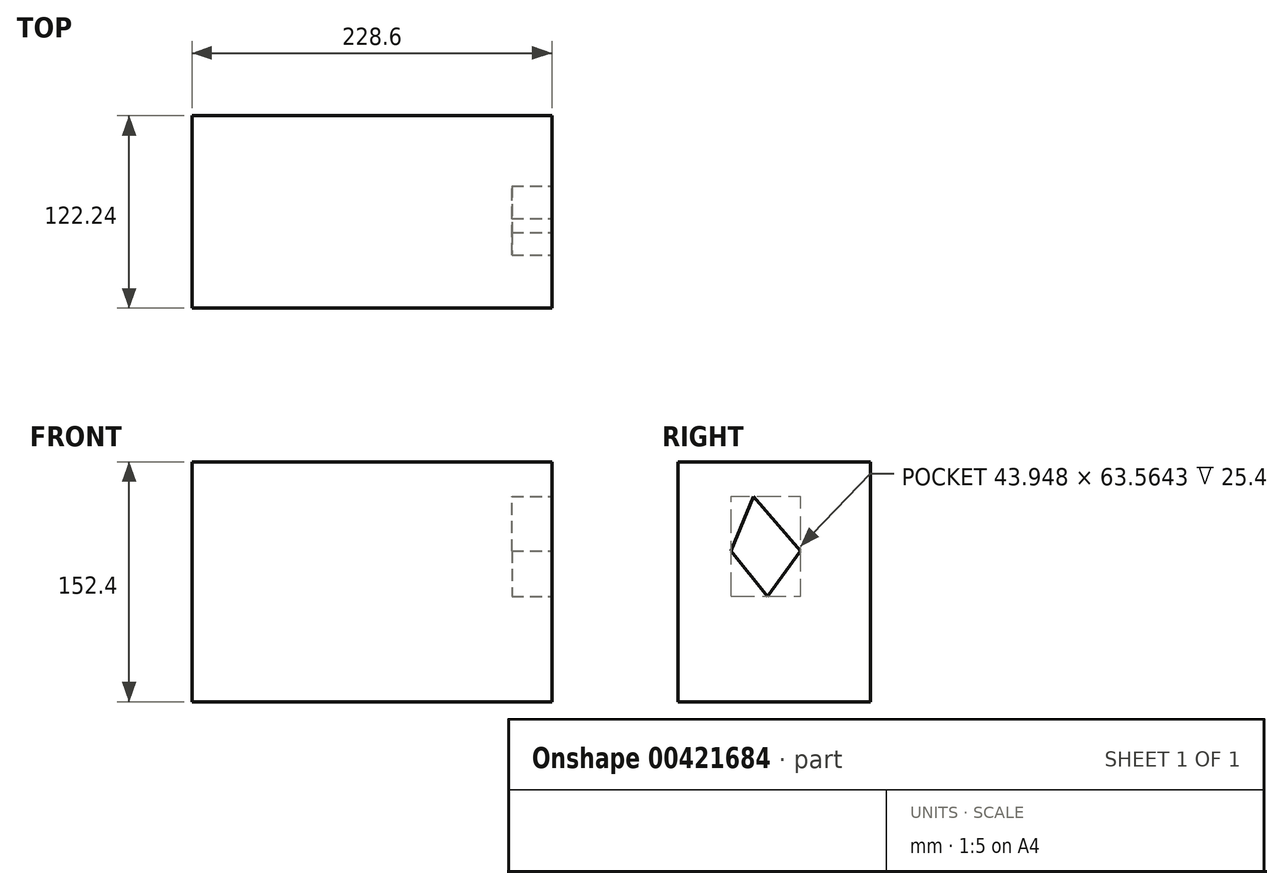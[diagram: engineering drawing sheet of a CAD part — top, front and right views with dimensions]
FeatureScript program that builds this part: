
annotation { "Feature Type Name" : "Feature", "Feature Type Description" : "" }
export const myFeature = defineFeature(function(context is Context, id is Id, definition is map)
    precondition{}
    {
        {
            var Q0;
            Q0=qCreatedBy(makeId("Right.planeOp"),FACE);
            var sketch = newSketch(context, id + "F0", { "sketchPlane" : qUnion([Q0])});
            skLineSegment(sketch, "E0", {"start": v(-51.89, 72.68) * mm, "end": v(-51.89, -79.72) * mm});
            skLineSegment(sketch, "E1", {"start": v(-51.89, 72.68) * mm, "end": v(70.35, 72.68) * mm});
            skLineSegment(sketch, "E2", {"start": v(70.35, 72.68) * mm, "end": v(70.35, -79.72) * mm});
            skLineSegment(sketch, "E3", {"start": v(70.35, -79.72) * mm, "end": v(-51.89, -79.72) * mm});
            skSolve(sketch);
        }
        {
            var Q0;
            Q0 = qSketchRegion(id + "F0", true);
            extrude(context, id + "F1", {"entities" : qUnion([Q0]), "depth" : 228.6 * mm});
        }
        {
            var Q0;
            Q0=makeQuery(id+"F1.opExtrude","CAP_FACE",FACE,{"disambiguationData":[OSD([sQuery(id+"F0.wireOp",EDGE,"E0"),sQuery(id+"F0.wireOp",EDGE,"E1"),sQuery(id+"F0.wireOp",EDGE,"E2"),sQuery(id+"F0.wireOp",EDGE,"E3")])],"isStart":false});
            var sketch = newSketch(context, id + "F2", { "sketchPlane" : qUnion([Q0])});
            skLineSegment(sketch, "E4", {"start": v(-3.77, 50.67) * mm, "end": v(-18.1, 15.97) * mm});
            skLineSegment(sketch, "E5", {"start": v(-18.1, 15.97) * mm, "end": v(5.1, -12.9) * mm});
            skLineSegment(sketch, "E6", {"start": v(5.1, -12.9) * mm, "end": v(25.84, 15.97) * mm});
            skLineSegment(sketch, "E7", {"start": v(25.84, 15.97) * mm, "end": v(-3.77, 50.67) * mm});
            skSolve(sketch);
        }
        {
            var Q0;
            Q0=makeQuery(id+"F2.imprint","IMPRINT",FACE,{"disambiguationData":[TD([[makeQuery(id+"F2.imprint","IMPRINT",EDGE,{"derivedFrom":sQuery(id+"F2.wireOp",EDGE,"E4")}),1.0]])]});
            extrude(context, id + "F3", {"entities" : qUnion([Q0]), "operationType" : NewBodyOperationType.REMOVE, "oppositeDirection" : true, "depth" : 25.4 * mm});
        }
    });
